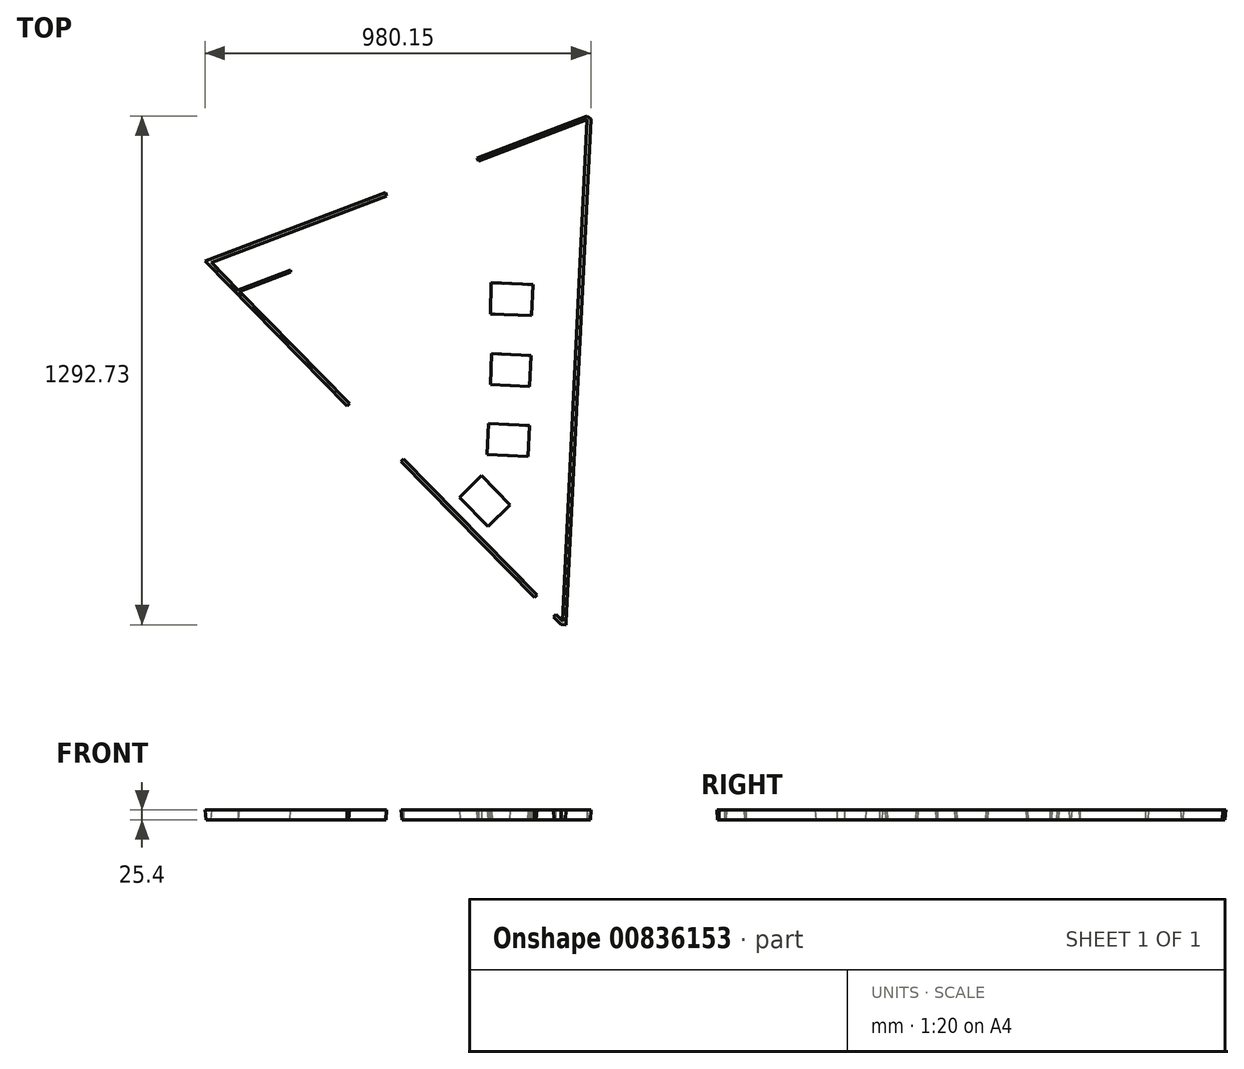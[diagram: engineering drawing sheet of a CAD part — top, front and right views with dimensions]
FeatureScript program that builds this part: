
annotation { "Feature Type Name" : "Feature", "Feature Type Description" : "" }
export const myFeature = defineFeature(function(context is Context, id is Id, definition is map)
    precondition{}
    {
        {
            var Q0;
            Q0=qCreatedBy(makeId("Top.planeOp"),FACE);
            var sketch = newSketch(context, id + "F0", { "sketchPlane" : qUnion([Q0])});
            skLineSegment(sketch, "E0", {"start": v(-416.86, -42.2) * mm, "end": v(-65.45, -401.1) * mm});
            skLineSegment(sketch, "E1", {"start": v(478.43, -956.57) * mm, "end": v(541.88, 322.34) * mm});
            skLineSegment(sketch, "E2", {"start": v(541.88, 322.34) * mm, "end": v(438.61, 283.07) * mm});
            skLineSegment(sketch, "E3", {"start": v(-347.07, -113.47) * mm, "end": v(-104.2, -21.13) * mm});
            skLineSegment(sketch, "E4", {"start": v(-136.7, 64.33) * mm, "end": v(-416.86, -42.2) * mm});
            skLineSegment(sketch, "E5", {"start": v(384.12, -860.25) * mm, "end": v(393.8, -650.25) * mm});
            skLineSegment(sketch, "E6", {"start": v(288.46, -711.4) * mm, "end": v(342.9, -658.1) * mm});
            skLineSegment(sketch, "E7", {"start": v(342.9, -658.1) * mm, "end": v(271.82, -585.5) * mm});
            skLineSegment(sketch, "E8", {"start": v(271.82, -585.5) * mm, "end": v(217.38, -638.81) * mm});
            skLineSegment(sketch, "E9", {"start": v(217.38, -638.81) * mm, "end": v(288.46, -711.4) * mm});
            skLineSegment(sketch, "E10", {"start": v(287.78, -529.2) * mm, "end": v(291.29, -453.08) * mm});
            skLineSegment(sketch, "E11", {"start": v(291.29, -453.08) * mm, "end": v(392.78, -457.75) * mm});
            skLineSegment(sketch, "E12", {"start": v(392.78, -457.75) * mm, "end": v(389.27, -533.87) * mm});
            skLineSegment(sketch, "E13", {"start": v(389.27, -533.87) * mm, "end": v(287.78, -529.2) * mm});
            skLineSegment(sketch, "E14", {"start": v(346.93, -353.93) * mm, "end": v(295.51, -351.56) * mm});
            skLineSegment(sketch, "E15", {"start": v(295.51, -351.56) * mm, "end": v(392.2, -356.02) * mm});
            skLineSegment(sketch, "E16", {"start": v(392.2, -356.02) * mm, "end": v(395.7, -279.9) * mm});
            skLineSegment(sketch, "E17", {"start": v(395.7, -279.9) * mm, "end": v(298.5, -275.42) * mm});
            skLineSegment(sketch, "E18", {"start": v(298.5, -275.42) * mm, "end": v(295.51, -351.56) * mm});
            skLineSegment(sketch, "E19", {"start": v(296.35, -171.98) * mm, "end": v(397.86, -176.17) * mm});
            skLineSegment(sketch, "E20", {"start": v(397.86, -176.17) * mm, "end": v(401.37, -100.05) * mm});
            skLineSegment(sketch, "E21", {"start": v(401.37, -100.05) * mm, "end": v(297.45, -95.26) * mm});
            skLineSegment(sketch, "E22", {"start": v(297.45, -95.26) * mm, "end": v(296.35, -171.98) * mm});
            skLineSegment(sketch, "E23", {"start": v(-214.76, -248.6) * mm, "end": v(-214.76, -166.14) * mm});
            skLineSegment(sketch, "E24", {"start": v(-104.2, -21.13) * mm, "end": v(-113.24, 2.6) * mm});
            skLineSegment(sketch, "E25", {"start": v(-136.7, 64.33) * mm, "end": v(-127.68, 40.59) * mm});
            skLineSegment(sketch, "E26", {"start": v(-136.7, 64.33) * mm, "end": v(29.49, 127.52) * mm});
            skLineSegment(sketch, "E27", {"start": v(438.61, 283.07) * mm, "end": v(264.52, 216.88) * mm});
            skLineSegment(sketch, "E28", {"start": v(-214.76, -248.6) * mm, "end": v(-65.45, -401.1) * mm});
            skLineSegment(sketch, "E29", {"start": v(384.12, -860.25) * mm, "end": v(74.26, -543.78) * mm});
            skLineSegment(sketch, "E30.trimOffspring", {"start": v(74.26, -543.78) * mm, "end": v(410.9, -887.6) * mm});
            skLineSegment(sketch, "E31", {"start": v(-214.76, -63.17) * mm, "end": v(-214.76, -127.52) * mm});
            skLineSegment(sketch, "E32", {"start": v(-214.76, -166.14) * mm, "end": v(-214.76, -248.6) * mm});
            skLineSegment(sketch, "E33.trimOffspring", {"start": v(-214.76, -127.52) * mm, "end": v(-214.76, -63.17) * mm});
            skLineSegment(sketch, "E34", {"start": v(530.3, 88.9) * mm, "end": v(466.43, 91.94) * mm});
            skLineSegment(sketch, "E35", {"start": v(524.07, -36.54) * mm, "end": v(461.49, -33.43) * mm});
            skLineSegment(sketch, "E36", {"start": v(478.43, -956.57) * mm, "end": v(460.66, -938.42) * mm});
            skLineSegment(sketch, "E37", {"start": v(410.9, -887.6) * mm, "end": v(384.12, -860.25) * mm});
            skLineSegment(sketch, "E38.trimOffspring", {"start": v(460.66, -938.42) * mm, "end": v(478.43, -956.57) * mm});
            skLineSegment(sketch, "E39", {"start": v(351.57, 249.98) * mm, "end": v(342.55, 114.05) * mm});
            skLineSegment(sketch, "E40", {"start": v(342.55, 114.05) * mm, "end": v(371.6, 112.71) * mm});
            skLineSegment(sketch, "E41.trimOffspring", {"start": v(412.2, 110.84) * mm, "end": v(430.64, 110) * mm});
            skLineSegment(sketch, "E42", {"start": v(110.71, -554.77) * mm, "end": v(183.66, -629.28) * mm});
            skLineSegment(sketch, "E43", {"start": v(211.67, -601.85) * mm, "end": v(138.9, -527.52) * mm});
            skLineSegment(sketch, "E44", {"start": v(138.9, -527.52) * mm, "end": v(110.71, -554.77) * mm});
            skLineSegment(sketch, "E45", {"start": v(401.4, -579.23) * mm, "end": v(496.93, -583.77) * mm});
            skPoint(sketch, "E46.start.orphan", {"position": v(428.1, 0) * mm});
            skLineSegment(sketch, "E47.trimOffspring", {"start": v(430.64, 110) * mm, "end": v(438.61, 283.07) * mm});
            skLineSegment(sketch, "E48", {"start": v(401.4, -579.23) * mm, "end": v(428.1, 0) * mm});
            skLineSegment(sketch, "E49", {"start": v(430.64, 110) * mm, "end": v(430.64, 77.14) * mm});
            skLineSegment(sketch, "E50.0", {"start": v(539.62, 328.27) * mm, "end": v(436.35, 289) * mm});
            skLineSegment(sketch, "E51.0", {"start": v(436.35, 289) * mm, "end": v(262.26, 222.82) * mm});
            skLineSegment(sketch, "E52.0", {"start": v(-138.96, 70.26) * mm, "end": v(27.23, 133.45) * mm});
            skLineSegment(sketch, "E53.0", {"start": v(-428.18, -39.7) * mm, "end": v(-69.99, -405.54) * mm});
            skLineSegment(sketch, "E53.1", {"start": v(-138.96, 70.26) * mm, "end": v(-428.18, -39.7) * mm});
            skLineSegment(sketch, "E54.0", {"start": v(69.72, -548.22) * mm, "end": v(406.37, -892.05) * mm});
            skLineSegment(sketch, "E55.0", {"start": v(473.9, -961.01) * mm, "end": v(456.12, -942.86) * mm});
            skLineSegment(sketch, "E56.0", {"start": v(484.77, -956.88) * mm, "end": v(548.22, 322.02) * mm});
            skLineSegment(sketch, "E57", {"start": v(-69.99, -405.54) * mm, "end": v(-65.45, -401.1) * mm});
            skLineSegment(sketch, "E58", {"start": v(69.72, -548.22) * mm, "end": v(74.26, -543.78) * mm});
            skLineSegment(sketch, "E59", {"start": v(406.37, -892.05) * mm, "end": v(410.9, -887.6) * mm});
            skLineSegment(sketch, "E60", {"start": v(456.12, -942.86) * mm, "end": v(460.66, -938.42) * mm});
            skLineSegment(sketch, "E61", {"start": v(473.9, -961.01) * mm, "end": v(478.43, -956.57) * mm});
            skLineSegment(sketch, "E62", {"start": v(473.9, -961.01) * mm, "end": v(484.93, -961.56) * mm});
            skLineSegment(sketch, "E63", {"start": v(484.93, -961.56) * mm, "end": v(484.77, -956.88) * mm});
            skLineSegment(sketch, "E64", {"start": v(548.22, 322.02) * mm, "end": v(539.62, 328.27) * mm});
            skLineSegment(sketch, "E65", {"start": v(264.52, 216.88) * mm, "end": v(262.26, 222.82) * mm});
            skLineSegment(sketch, "E66", {"start": v(29.49, 127.52) * mm, "end": v(27.23, 133.45) * mm});
            skLineSegment(sketch, "E67.0", {"start": v(-134.33, 65.23) * mm, "end": v(-125.3, 41.49) * mm});
            skLineSegment(sketch, "E68.0", {"start": v(-101.84, -20.23) * mm, "end": v(-110.86, 3.51) * mm});
            skLineSegment(sketch, "E69.0", {"start": v(-346.16, -115.85) * mm, "end": v(-103.3, -23.5) * mm});
            skLineSegment(sketch, "E70.0", {"start": v(-212.22, -63.17) * mm, "end": v(-212.22, -127.52) * mm});
            skLineSegment(sketch, "E71.0", {"start": v(-212.22, -166.14) * mm, "end": v(-212.22, -248.6) * mm});
            skLineSegment(sketch, "E72.0", {"start": v(398.87, -579.11) * mm, "end": v(425.56, 0.12) * mm});
            skSolve(sketch);
        }
        {
            var Q0;
            Q0 = qSketchRegion(id + "F0", true);
            extrude(context, id + "F1", {"entities" : qUnion([Q0]), "depth" : 25.4 * mm, "offsetDistance" : 25.4 * mm, "hasDraft" : true, "draftAngle" : 3 * degree});
        }
    });
